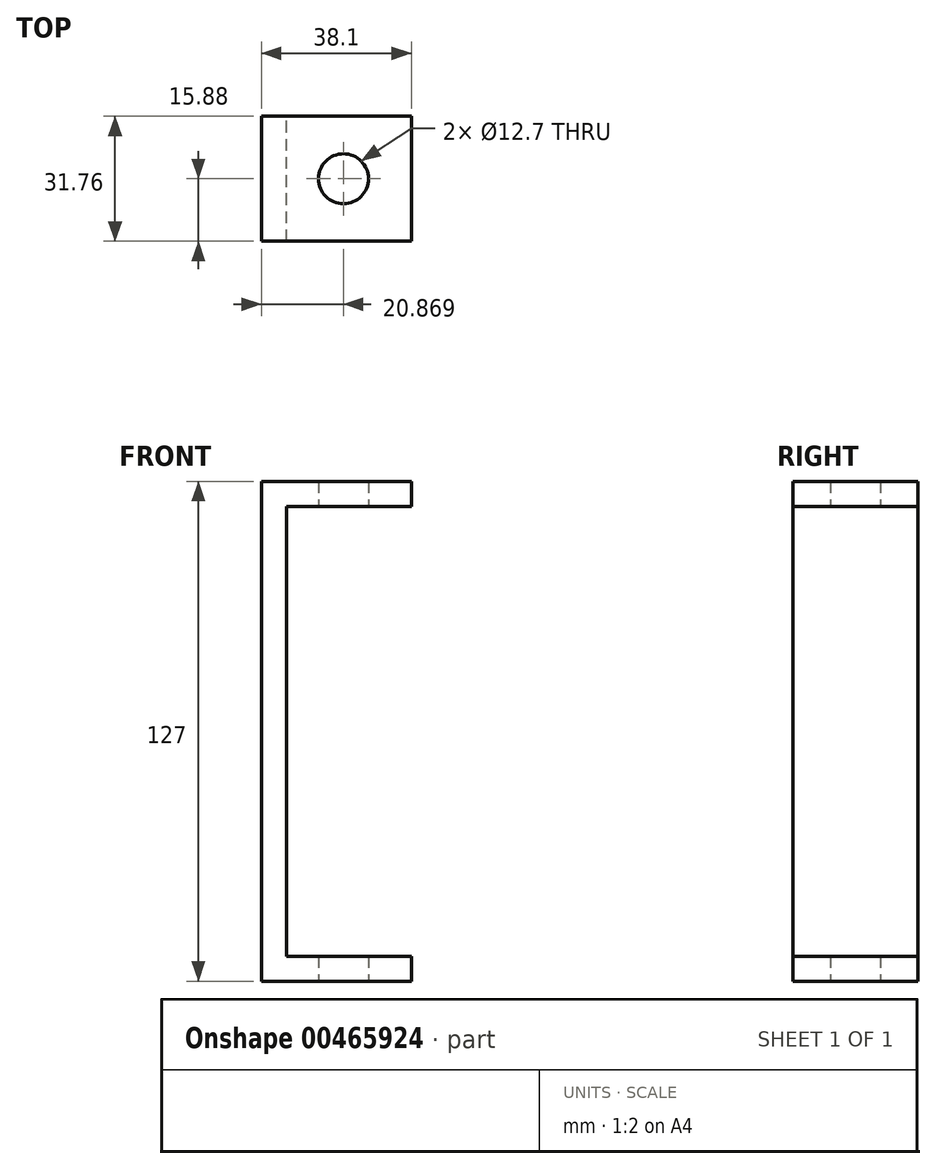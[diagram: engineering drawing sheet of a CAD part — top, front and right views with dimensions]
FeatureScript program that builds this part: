
annotation { "Feature Type Name" : "Feature", "Feature Type Description" : "" }
export const myFeature = defineFeature(function(context is Context, id is Id, definition is map)
    precondition{}
    {
        {
            var Q0;
            Q0=qCreatedBy(makeId("Front.planeOp"),FACE);
            var sketch = newSketch(context, id + "F0", { "sketchPlane" : qUnion([Q0])});
            skLineSegment(sketch, "E0.bottom", {"start": v(-3.17, 63.5) * mm, "end": v(3.18, 63.5) * mm});
            skLineSegment(sketch, "E0.top", {"start": v(-3.17, -63.5) * mm, "end": v(3.18, -63.5) * mm});
            skLineSegment(sketch, "E0.left", {"start": v(-3.17, 63.5) * mm, "end": v(-3.17, -63.5) * mm});
            skLineSegment(sketch, "E0.right", {"start": v(3.18, 63.5) * mm, "end": v(3.18, -63.5) * mm});
            skPoint(sketch, "E0.middle", {"position": v(0, 0) * mm});
            skLineSegment(sketch, "E1.bottom", {"start": v(3.18, 63.5) * mm, "end": v(34.93, 63.5) * mm});
            skLineSegment(sketch, "E1.top", {"start": v(3.18, 57.15) * mm, "end": v(34.93, 57.15) * mm});
            skLineSegment(sketch, "E1.left", {"start": v(3.18, 63.5) * mm, "end": v(3.18, 57.15) * mm});
            skLineSegment(sketch, "E1.right", {"start": v(34.93, 63.5) * mm, "end": v(34.93, 57.15) * mm});
            skLineSegment(sketch, "E2.bottom", {"start": v(3.18, -63.5) * mm, "end": v(34.93, -63.5) * mm});
            skLineSegment(sketch, "E2.top", {"start": v(3.18, -57.15) * mm, "end": v(34.93, -57.15) * mm});
            skLineSegment(sketch, "E2.left", {"start": v(3.18, -63.5) * mm, "end": v(3.18, -57.15) * mm});
            skLineSegment(sketch, "E2.right", {"start": v(34.93, -63.5) * mm, "end": v(34.93, -57.15) * mm});
            skSolve(sketch);
        }
        {
            var Q0;
            Q0=makeQuery(id+"F0.imprint","IMPRINT",FACE,{"disambiguationData":[TD([[makeQuery(id+"F0.imprint","IMPRINT",EDGE,{"derivedFrom":sQuery(id+"F0.wireOp",EDGE,"E2.bottom")}),1.0]])]});
            var Q1;
            Q1=makeQuery(id+"F0.imprint","IMPRINT",FACE,{"disambiguationData":[TD([[makeQuery(id+"F0.imprint","IMPRINT",EDGE,{"derivedFrom":sQuery(id+"F0.wireOp",EDGE,"E0.bottom")}),-1.0]])]});
            var Q2;
            Q2=makeQuery(id+"F0.imprint","IMPRINT",FACE,{"disambiguationData":[TD([[makeQuery(id+"F0.imprint","IMPRINT",EDGE,{"derivedFrom":sQuery(id+"F0.wireOp",EDGE,"E1.bottom")}),-1.0]])]});
            extrude(context, id + "F1", {"entities" : qUnion([Q0, Q1, Q2]), "endBound" : BoundingType.SYMMETRIC, "depth" : 31.75 * mm});
        }
        {
            var Q0;
            Q0=qCreatedBy(makeId("Top.planeOp"),FACE);
            var sketch = newSketch(context, id + "F2", { "sketchPlane" : qUnion([Q0])});
            skLineSegment(sketch, "E3", {"start": v(36.74, 0) * mm, "end": v(17.69, 0) * mm});
            skCircle(sketch, "E4", {"center": v(17.69, 0) * mm, "radius": 6.35 * mm});
            skSolve(sketch);
        }
        {
            var Q0;
            Q0=makeQuery(id+"F2.imprint","IMPRINT",FACE,{"disambiguationData":[TD([[makeQuery(id+"F2.imprint","IMPRINT",EDGE,{"derivedFrom":sQuery(id+"F2.wireOp",EDGE,"E4")}),1.0]])]});
            extrude(context, id + "F3", {"entities" : qUnion([Q0]), "operationType" : NewBodyOperationType.REMOVE, "endBound" : BoundingType.SYMMETRIC, "depth" : 254 * mm});
        }
    });
